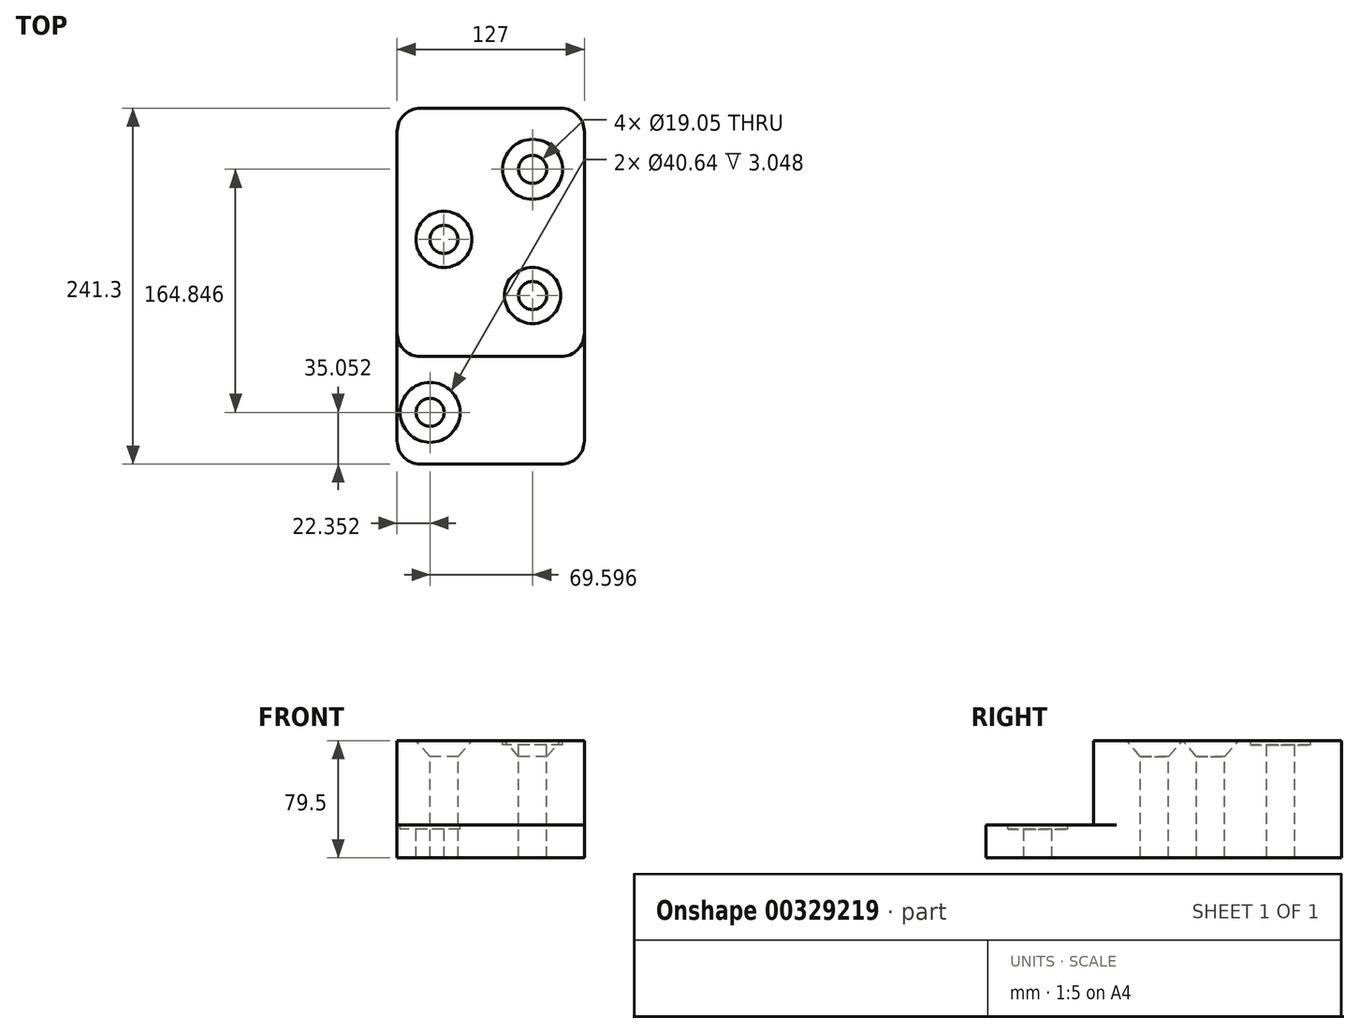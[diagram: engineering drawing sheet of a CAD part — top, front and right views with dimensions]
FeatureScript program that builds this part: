
annotation { "Feature Type Name" : "Feature", "Feature Type Description" : "" }
export const myFeature = defineFeature(function(context is Context, id is Id, definition is map)
    precondition{}
    {
        {
            var Q0;
            Q0=qCreatedBy(makeId("Right.planeOp"),FACE);
            var sketch = newSketch(context, id + "F0", { "sketchPlane" : qUnion([Q0])});
            skLineSegment(sketch, "E0.bottom", {"start": v(0, 0) * mm, "end": v(241.3, 0) * mm});
            skLineSegment(sketch, "E0.top", {"start": v(0, 22.35) * mm, "end": v(241.3, 22.35) * mm});
            skLineSegment(sketch, "E0.left", {"start": v(0, 0) * mm, "end": v(0, 22.35) * mm});
            skLineSegment(sketch, "E0.right", {"start": v(241.3, 0) * mm, "end": v(241.3, 22.35) * mm});
            skLineSegment(sketch, "E1.bottom", {"start": v(72.9, 0) * mm, "end": v(241.3, 0) * mm});
            skLineSegment(sketch, "E1.top", {"start": v(72.9, 79.5) * mm, "end": v(241.3, 79.5) * mm});
            skLineSegment(sketch, "E1.left", {"start": v(72.9, 0) * mm, "end": v(72.9, 79.5) * mm});
            skLineSegment(sketch, "E1.right", {"start": v(241.3, 0) * mm, "end": v(241.3, 79.5) * mm});
            skSolve(sketch);
        }
        {
            var Q0;
            Q0 = qSketchRegion(id + "F0", true);
            extrude(context, id + "F1", {"entities" : qUnion([Q0]), "depth" : 127 * mm});
        }
        {
            var Q0;
            Q0=makeQuery(id+"F1.opExtrude","CAP_EDGE",EDGE,{"disambiguationData":[OSD([sQuery(id+"F0.wireOp",EDGE,"E1.left")])],"isStart":false});
            var Q1;
            Q1=makeQuery(id+"F1.opExtrude","CAP_EDGE",EDGE,{"disambiguationData":[OSD([sQuery(id+"F0.wireOp",EDGE,"E0.left")])],"isStart":false});
            var Q2;
            Q2=makeQuery(id+"F1.opExtrude","CAP_EDGE",EDGE,{"disambiguationData":[OSD([sQuery(id+"F0.wireOp",EDGE,"E1.right")])],"isStart":false});
            var Q3;
            Q3=makeQuery(id+"F1.opExtrude","CAP_EDGE",EDGE,{"disambiguationData":[OSD([sQuery(id+"F0.wireOp",EDGE,"E1.left")])],"isStart":true});
            var Q4;
            Q4=makeQuery(id+"F1.opExtrude","CAP_EDGE",EDGE,{"disambiguationData":[OSD([sQuery(id+"F0.wireOp",EDGE,"E0.left")])],"isStart":true});
            var Q5;
            Q5=makeQuery(id+"F1.opExtrude","CAP_EDGE",EDGE,{"disambiguationData":[OSD([sQuery(id+"F0.wireOp",EDGE,"E1.right")])],"isStart":true});
            fillet(context, id + "F2", {"entities" : qUnion([Q0, Q1, Q2, Q3, Q4, Q5]), "radius" : 15.75 * mm, "tangentPropagation" : true, "allowEdgeOverflow" : false});
        }
        {
            var Q0;
            Q0=makeQuery(id+"F1.opExtrude","SWEPT_FACE",FACE,{"disambiguationData":[OSD([sQuery(id+"F0.wireOp",EDGE,"E1.top")])]});
            var sketch = newSketch(context, id + "F3", { "sketchPlane" : qUnion([Q0])});
            skPoint(sketch, "E2", {"position": v(91.95, 199.9) * mm});
            skPoint(sketch, "E3", {"position": v(31.75, 152.4) * mm});
            skPoint(sketch, "E4", {"position": v(91.95, 114.3) * mm});
            skPoint(sketch, "E5", {"position": v(22.35, 35.05) * mm});
            skSolve(sketch);
        }
        {
            var Q0;
            Q0=sQuery(id+"F3.wireOp",VERTEX,"E3");
            var Q1;
            Q1=sQuery(id+"F3.wireOp",VERTEX,"E4");
            var Q2;
            Q2=makeQuery(id+"F1.opExtrude","SWEPT_BODY",BODY,{"disambiguationData":[OSD([sQuery(id+"F0.wireOp",EDGE,"E0.bottom"),sQuery(id+"F0.wireOp",EDGE,"E0.top"),sQuery(id+"F0.wireOp",EDGE,"E0.left"),sQuery(id+"F0.wireOp",EDGE,"E1.bottom"),sQuery(id+"F0.wireOp",EDGE,"E1.top"),sQuery(id+"F0.wireOp",EDGE,"E1.left"),sQuery(id+"F0.wireOp",EDGE,"E1.right")])]});
            hole(context, id + "F4", {"style" : HoleStyle.C_SINK, "endStyle" : HoleEndStyle.THROUGH, "holeDiameter" : 19.05 * mm, "cSinkDiameter" : 38.1 * mm, "cSinkAngle" : 82 * degree, "tappedDepth" : 12.7 * mm, "tapClearance" : 3, "locations" : qUnion([Q0, Q1]), "scope" : qUnion([Q2])});
        }
        {
            var Q0;
            Q0=sQuery(id+"F3.wireOp",VERTEX,"E2");
            var Q1;
            Q1=sQuery(id+"F3.wireOp",VERTEX,"E5");
            var Q2;
            Q2=makeQuery(id+"F1.opExtrude","SWEPT_BODY",BODY,{"disambiguationData":[OSD([sQuery(id+"F0.wireOp",EDGE,"E0.bottom"),sQuery(id+"F0.wireOp",EDGE,"E0.top"),sQuery(id+"F0.wireOp",EDGE,"E0.left"),sQuery(id+"F0.wireOp",EDGE,"E1.bottom"),sQuery(id+"F0.wireOp",EDGE,"E1.top"),sQuery(id+"F0.wireOp",EDGE,"E1.left"),sQuery(id+"F0.wireOp",EDGE,"E1.right")])]});
            hole(context, id + "F5", {"style" : HoleStyle.C_BORE, "endStyle" : HoleEndStyle.THROUGH, "holeDiameter" : 19.05 * mm, "cBoreDiameter" : 40.64 * mm, "cBoreDepth" : 3.05 * mm, "tappedDepth" : 12.7 * mm, "tapClearance" : 3, "locations" : qUnion([Q0, Q1]), "scope" : qUnion([Q2])});
        }
    });
